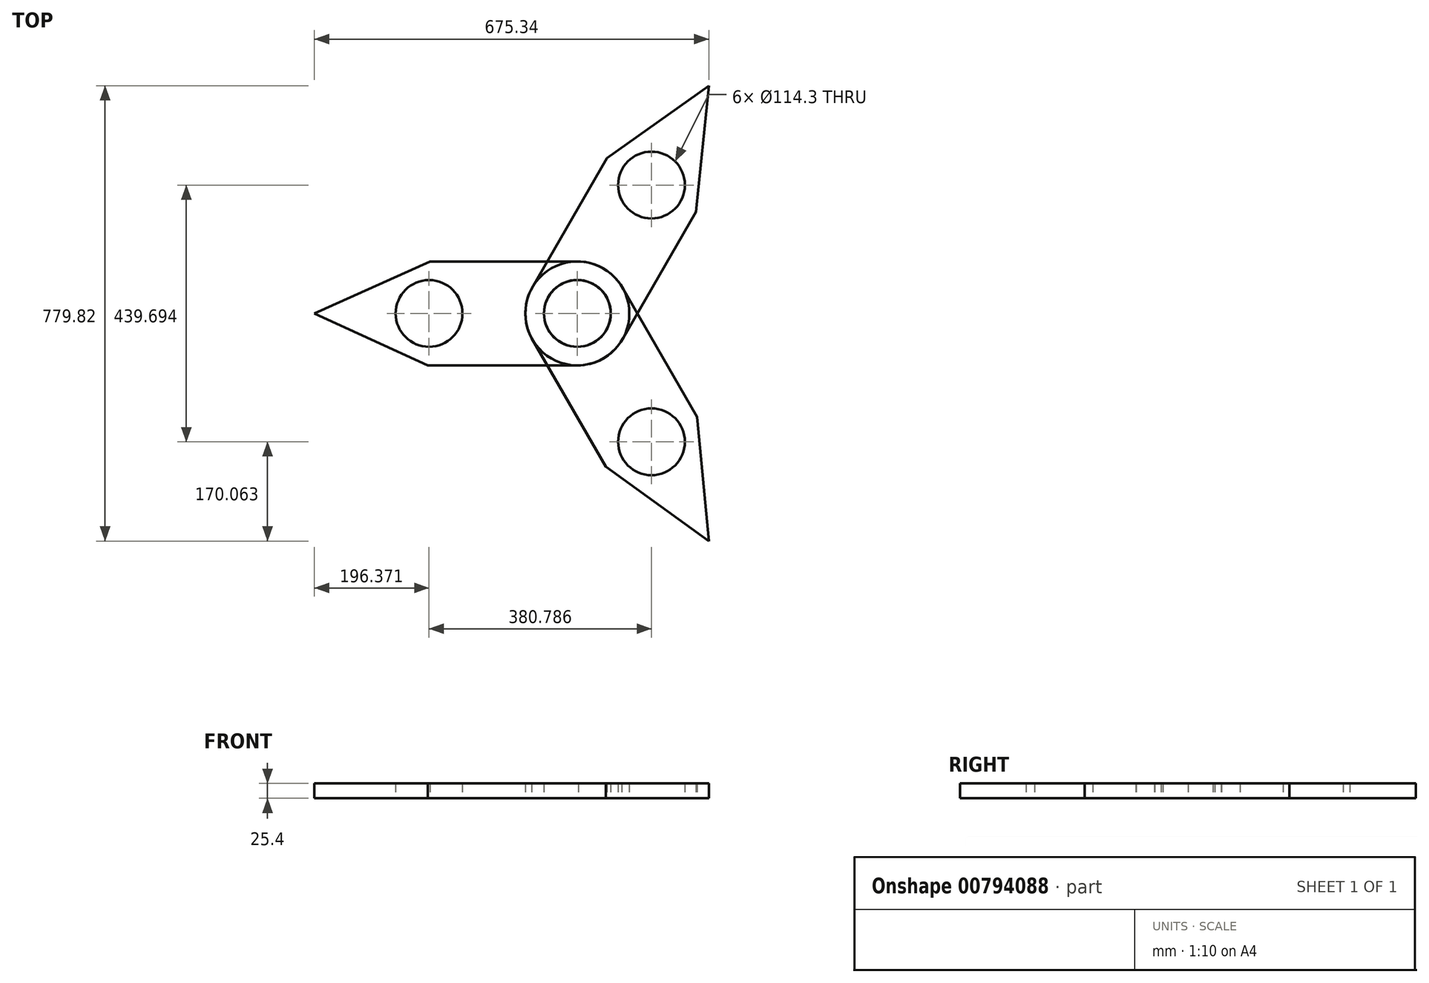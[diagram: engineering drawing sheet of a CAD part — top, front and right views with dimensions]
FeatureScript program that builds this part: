
annotation { "Feature Type Name" : "Feature", "Feature Type Description" : "" }
export const myFeature = defineFeature(function(context is Context, id is Id, definition is map)
    precondition{}
    {
        {
            var Q0;
            Q0=qCreatedBy(makeId("Top.planeOp"),FACE);
            var sketch = newSketch(context, id + "F0", { "sketchPlane" : qUnion([Q0])});
            skCircle(sketch, "E0", {"center": v(230.12, 0) * mm, "radius": 88.9 * mm});
            skLineSegment(sketch, "E1", {"start": v(-21.99, 88.88) * mm, "end": v(232.01, 88.88) * mm});
            skLineSegment(sketch, "E2", {"start": v(232.01, -88.88) * mm, "end": v(-25.77, -88.88) * mm});
            skCircle(sketch, "E3", {"center": v(-23.88, 0) * mm, "radius": 57.15 * mm});
            skCircle(sketch, "E4", {"center": v(230.12, 0) * mm, "radius": 57.15 * mm});
            skLineSegment(sketch, "E5", {"start": v(-25.77, -88.88) * mm, "end": v(-220.25, 0) * mm});
            skLineSegment(sketch, "E6", {"start": v(-220.25, 0) * mm, "end": v(-21.99, 88.88) * mm});
            skArc(sketch, "E7.trimOffspring", {"start": v(-25.77, -88.88) * mm, "mid": v(65, -1.9) * mm, "end": v(-21.99, 88.88) * mm});
            skSolve(sketch);
        }
        {
            var Q0;
            Q0=qCreatedBy(makeId("Front.planeOp"),FACE);
            var sketch = newSketch(context, id + "F1", { "sketchPlane" : qUnion([Q0])});
            skLineSegment(sketch, "E8", {"start": v(229.98, 0) * mm, "end": v(229.98, 70.53) * mm});
            skSolve(sketch);
        }
        {
            var Q0;
            {var subQ0=sQuery(id+"F0.wireOp",EDGE,"E1");var subQ1=sQuery(id+"F0.wireOp",EDGE,"E0");var subQ2=makeQuery(id+"F0.imprint","INTERSECT",VERTEX,{"disambiguationData":[OD(1.0)],"derivedFrom":[subQ1,subQ0]});Q0=makeQuery(id+"F0.imprint","IMPRINT",FACE,{"disambiguationData":[TD([[makeQuery(id+"F0.imprint","IMPRINT",EDGE,{"disambiguationData":[TD([[subQ2,-1.0]])],"derivedFrom":subQ1}),-1.0]])]});}
            var Q1;
            Q1=makeQuery(id+"F0.imprint","IMPRINT",FACE,{"disambiguationData":[TD([[makeQuery(id+"F0.imprint","IMPRINT",EDGE,{"derivedFrom":sQuery(id+"F0.wireOp",EDGE,"E3")}),-1.0]])]});
            var Q2;
            Q2=makeQuery(id+"F0.imprint","IMPRINT",FACE,{"disambiguationData":[TD([[makeQuery(id+"F0.imprint","IMPRINT",EDGE,{"derivedFrom":sQuery(id+"F0.wireOp",EDGE,"E4")}),-1.0]])]});
            extrude(context, id + "F2", {"entities" : qUnion([Q0, Q1, Q2]), "depth" : 25.4 * mm, "offsetDistance" : 25.4 * mm});
        }
        {
            var Q0;
            Q0=makeQuery(id+"F2.opExtrude","SWEPT_BODY",BODY,{"disambiguationData":[OSD([sQuery(id+"F0.wireOp",EDGE,"E0"),sQuery(id+"F0.wireOp",EDGE,"E1"),sQuery(id+"F0.wireOp",EDGE,"E2"),sQuery(id+"F0.wireOp",EDGE,"E3"),sQuery(id+"F0.wireOp",EDGE,"E4"),sQuery(id+"F0.wireOp",EDGE,"E5"),sQuery(id+"F0.wireOp",EDGE,"E6")])]});
            var Q1;
            Q1=sQuery(id+"F1.wireOp",EDGE,"E8");
            circularPattern(context, id + "F3", {"entities" : qUnion([Q0]), "axis" : qUnion([Q1]), "angle" : 360 * degree, "instanceCount" : 3, "equalSpace" : true});
        }
    });
